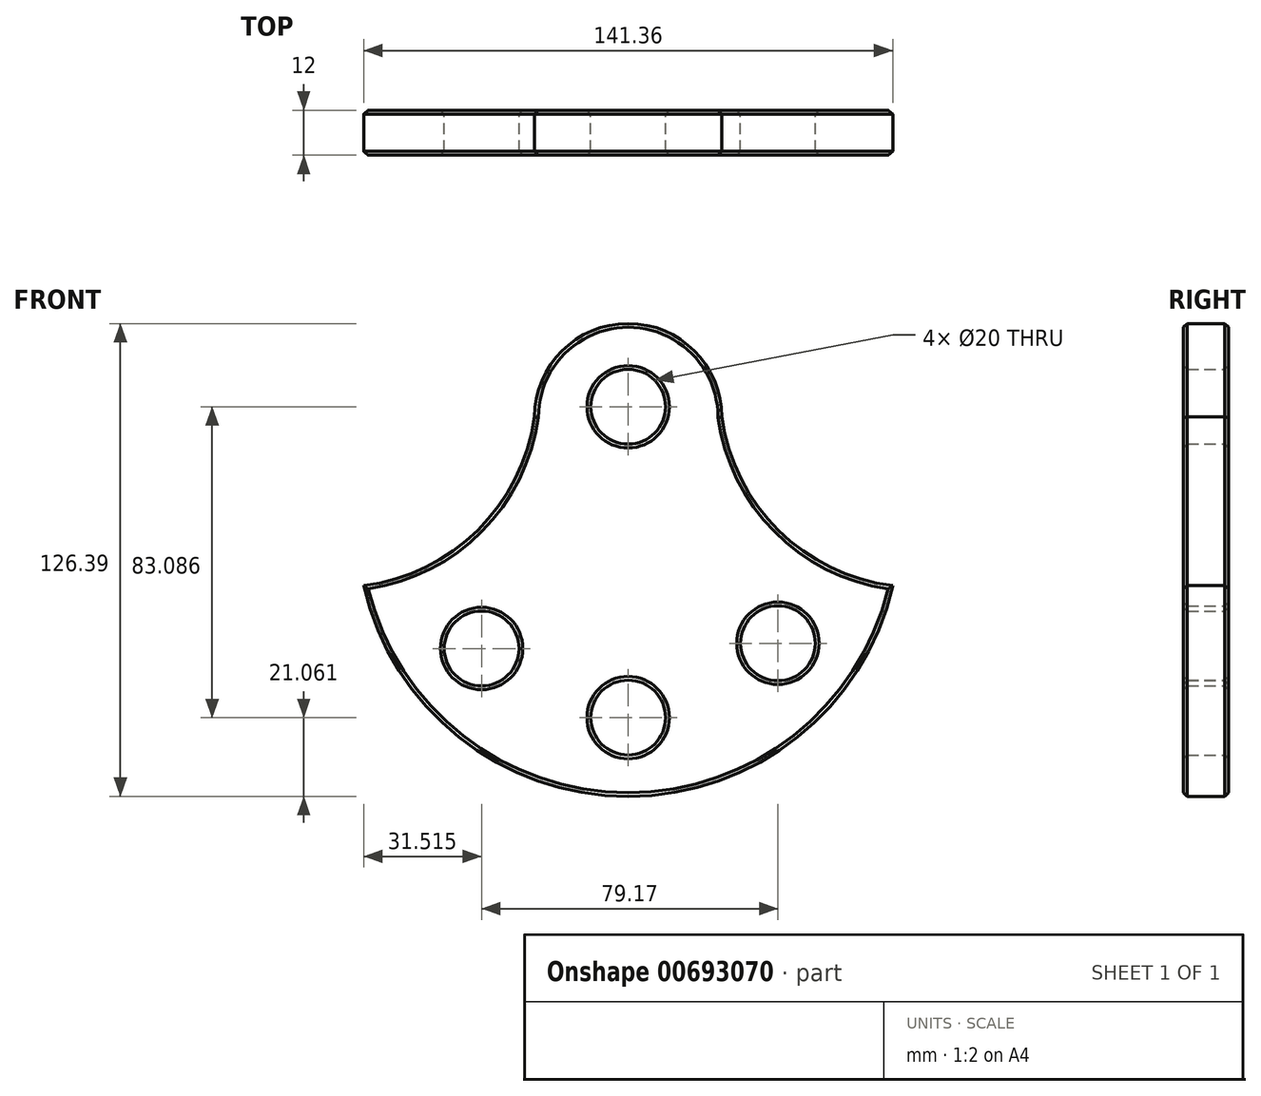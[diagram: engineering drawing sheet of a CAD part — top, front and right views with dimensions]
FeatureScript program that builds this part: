
annotation { "Feature Type Name" : "Feature", "Feature Type Description" : "" }
export const myFeature = defineFeature(function(context is Context, id is Id, definition is map)
    precondition{}
    {
        {
            var Q0;
            Q0=qCreatedBy(makeId("Front.planeOp"),FACE);
            var sketch = newSketch(context, id + "F0", { "sketchPlane" : qUnion([Q0])});
            skCircle(sketch, "E0", {"center": v(0, 0) * mm, "radius": 70.68 * mm});
            skCircle(sketch, "E1", {"center": v(0, 45.08) * mm, "radius": 25 * mm});
            skLineSegment(sketch, "E2", {"start": v(-25, 45.08) * mm, "end": v(25, 45.08) * mm});
            skArc(sketch, "E3", {"start": v(25, 45.08) * mm, "mid": v(40.16, 14.76) * mm, "end": v(70.68, 0) * mm});
            skArc(sketch, "E4", {"start": v(-70.68, 0) * mm, "mid": v(-40.2, 14.8) * mm, "end": v(-25, 45.08) * mm});
            skArc(sketch, "E5", {"start": v(-70.68, 0) * mm, "mid": v(0, -56.31) * mm, "end": v(70.68, 0) * mm});
            skSolve(sketch);
        }
        {
            var Q0;
            {var subQ3=sQuery(id+"F0.wireOp",EDGE,"E3");Q0=makeQuery(id+"F0.imprint","IMPRINT",FACE,{"disambiguationData":[TD([[makeQuery(id+"F0.imprint","IMPRINT",EDGE,{"derivedFrom":subQ3}),-1.0]])]});}
            var Q1;
            {var subQ0=sQuery(id+"F0.wireOp",EDGE,"E2");Q1=makeQuery(id+"F0.imprint","IMPRINT",FACE,{"disambiguationData":[TD([[makeQuery(id+"F0.imprint","IMPRINT",EDGE,{"derivedFrom":subQ0}),-1.0]])]});}
            var Q2;
            {var subQ0=sQuery(id+"F0.wireOp",EDGE,"E2");Q2=makeQuery(id+"F0.imprint","IMPRINT",FACE,{"disambiguationData":[TD([[makeQuery(id+"F0.imprint","IMPRINT",EDGE,{"derivedFrom":subQ0}),1.0]])]});}
            extrude(context, id + "F1", {"entities" : qUnion([Q0, Q1, Q2]), "depth" : 12 * mm, "offsetDistance" : 25 * mm});
        }
        {
            var Q0;
            Q0=makeQuery(id+"F1.opExtrude","CAP_FACE",FACE,{"disambiguationData":[OSD([sQuery(id+"F0.wireOp",EDGE,"E1"),sQuery(id+"F0.wireOp",EDGE,"E3"),sQuery(id+"F0.wireOp",EDGE,"E4"),sQuery(id+"F0.wireOp",EDGE,"E5")])],"isStart":true});
            var sketch = newSketch(context, id + "F2", { "sketchPlane" : qUnion([Q0])});
            skCircle(sketch, "E6", {"center": v(0, -35.25) * mm, "radius": 12.1 * mm});
            skCircle(sketch, "E7", {"center": v(-40, -15.39) * mm, "radius": 11.6 * mm});
            skCircle(sketch, "E8", {"center": v(39.17, -16.79) * mm, "radius": 11.3 * mm});
            skCircle(sketch, "E9", {"center": v(0, 47.84) * mm, "radius": 9.56 * mm});
            skSolve(sketch);
        }
        {
            var Q0;
            Q0=sQuery(id+"F2.wireOp",VERTEX,"E7.center");
            var Q1;
            Q1=sQuery(id+"F2.wireOp",VERTEX,"E6.center");
            var Q2;
            Q2=sQuery(id+"F2.wireOp",VERTEX,"E8.center");
            var Q3;
            Q3=sQuery(id+"F2.wireOp",VERTEX,"E9.center");
            var Q4;
            Q4=makeQuery(id+"F1.opExtrude","SWEPT_BODY",BODY,{"disambiguationData":[OSD([sQuery(id+"F0.wireOp",EDGE,"E1"),sQuery(id+"F0.wireOp",EDGE,"E3"),sQuery(id+"F0.wireOp",EDGE,"E4"),sQuery(id+"F0.wireOp",EDGE,"E5")])]});
            hole(context, id + "F3", {"style" : HoleStyle.SIMPLE, "endStyle" : HoleEndStyle.THROUGH, "holeDiameter" : 20 * mm, "majorDiameter" : 5 * mm, "isTappedThrough" : true, "tappedDepth" : 12 * mm, "tapClearance" : 3, "locations" : qUnion([Q0, Q1, Q2, Q3]), "scope" : qUnion([Q4])});
        }
        {
            var Q0;
            Q0=makeQuery(id+"F1.opExtrude","CAP_FACE",FACE,{"disambiguationData":[OSD([sQuery(id+"F0.wireOp",EDGE,"E1"),sQuery(id+"F0.wireOp",EDGE,"E3"),sQuery(id+"F0.wireOp",EDGE,"E4"),sQuery(id+"F0.wireOp",EDGE,"E5")])],"isStart":true});
            chamfer(context, id + "F4", {"entities" : qUnion([Q0]), "width" : 1 * mm, "tangentPropagation" : true});
        }
        {
            var Q0;
            Q0=makeQuery(id+"F1.opExtrude","CAP_FACE",FACE,{"disambiguationData":[OSD([sQuery(id+"F0.wireOp",EDGE,"E1"),sQuery(id+"F0.wireOp",EDGE,"E3"),sQuery(id+"F0.wireOp",EDGE,"E4"),sQuery(id+"F0.wireOp",EDGE,"E5")])],"isStart":false});
            chamfer(context, id + "F5", {"entities" : qUnion([Q0]), "width" : 1 * mm, "tangentPropagation" : true});
        }
    });
